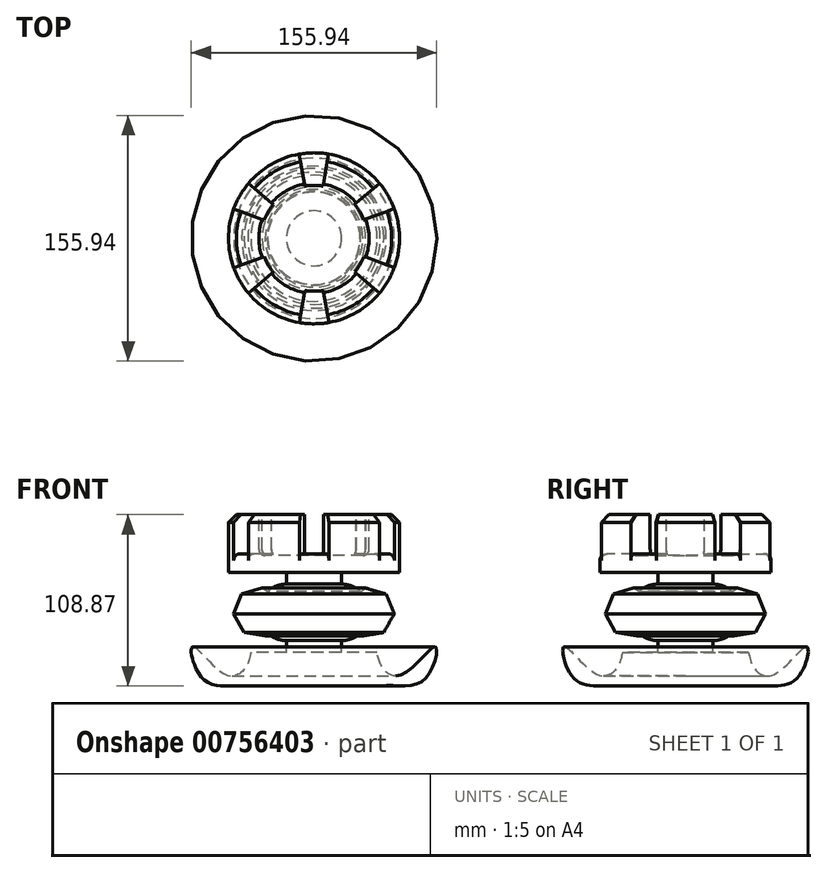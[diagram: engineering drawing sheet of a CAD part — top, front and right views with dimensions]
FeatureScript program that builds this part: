
annotation { "Feature Type Name" : "Feature", "Feature Type Description" : "" }
export const myFeature = defineFeature(function(context is Context, id is Id, definition is map)
    precondition{}
    {
        {
            var Q0;
            Q0=qCreatedBy(makeId("Front.planeOp"),FACE);
            var sketch = newSketch(context, id + "F0", { "sketchPlane" : qUnion([Q0])});
            skLineSegment(sketch, "E0", {"start": v(0, 0) * mm, "end": v(42.03, 0) * mm});
            skLineSegment(sketch, "E1", {"start": v(40.1, 21.45) * mm, "end": v(17.5, 21.45) * mm});
            skLineSegment(sketch, "E2", {"start": v(17.5, 21.45) * mm, "end": v(17.5, 28.86) * mm});
            skLineSegment(sketch, "E3", {"start": v(0, 108.87) * mm, "end": v(0, 0) * mm});
            skLineSegment(sketch, "E4", {"start": v(0, 108.87) * mm, "end": v(54.3, 108.87) * mm});
            skLineSegment(sketch, "E5", {"start": v(54.3, 108.87) * mm, "end": v(54.3, 72.1) * mm});
            skLineSegment(sketch, "E6", {"start": v(17.5, 72.1) * mm, "end": v(54.3, 72.1) * mm});
            skArc(sketch, "E7", {"start": v(17.5, 28.86) * mm, "mid": v(23.84, 30.02) * mm, "end": v(29.36, 33.35) * mm});
            skLineSegment(sketch, "E8.trimOffspring", {"start": v(17.5, 64.7) * mm, "end": v(17.5, 72.1) * mm});
            skLineSegment(sketch, "E9.0", {"start": v(50.96, 45.83) * mm, "end": v(44.36, 34.03) * mm});
            skLineSegment(sketch, "E9.1", {"start": v(44.36, 34.03) * mm, "end": v(31.03, 31.84) * mm});
            skLineSegment(sketch, "E9.2", {"start": v(31.03, 31.84) * mm, "end": v(29.36, 33.35) * mm});
            skLineSegment(sketch, "E9.4", {"start": v(29.7, 59.9) * mm, "end": v(32.89, 62.14) * mm});
            skLineSegment(sketch, "E9.5", {"start": v(32.89, 62.14) * mm, "end": v(45.85, 58.33) * mm});
            skLineSegment(sketch, "E9.6", {"start": v(45.85, 58.33) * mm, "end": v(50.96, 45.83) * mm});
            skPoint(sketch, "E9.0.midPoint", {"position": v(47.66, 39.93) * mm});
            skPoint(sketch, "E9.cCircle.center.orphan", {"position": v(35.42, 46.78) * mm});
            skArc(sketch, "E10.trimOffspring", {"start": v(29.7, 59.9) * mm, "mid": v(24.05, 63.45) * mm, "end": v(17.5, 64.7) * mm});
            skFitSpline(sketch, "E11", {"points": [v(42.03, 0) * mm, v(70.48, 4.44) * mm, v(77.04, 24.86) * mm, v(54.31, 6.63) * mm, v(40.1, 21.45) * mm], "startDerivative": vector(116, 13.94) * mm, "endDerivative": vector(-11.66, 114.4) * mm});
            skSolve(sketch);
        }
        {
            var Q0;
            Q0=makeQuery(id+"F0.imprint","IMPRINT",FACE,{"disambiguationData":[TD([[makeQuery(id+"F0.imprint","IMPRINT",EDGE,{"derivedFrom":sQuery(id+"F0.wireOp",EDGE,"E0")}),1.0]])]});
            var Q1;
            Q1=sQuery(id+"F0.wireOp",EDGE,"E3");
            revolve(context, id + "F1", {"surfaceOperationType" : NewSurfaceOperationType.NEW, "entities" : qUnion([Q0]), "axis" : qUnion([Q1]), "revolveType" : RevolveType.FULL});
        }
        {
            var Q0;
            Q0=makeQuery(id+"F1.opRevolve","SWEPT_FACE",FACE,{"disambiguationData":[OSD([sQuery(id+"F0.wireOp",EDGE,"E4")])]});
            var sketch = newSketch(context, id + "F2", { "sketchPlane" : qUnion([Q0])});
            skCircle(sketch, "E12", {"center": v(0, 0) * mm, "radius": 35 * mm});
            skSolve(sketch);
        }
        {
            var Q0;
            Q0=makeQuery(id+"F2.imprint","IMPRINT",FACE,{"disambiguationData":[TD([[makeQuery(id+"F2.imprint","IMPRINT",EDGE,{"derivedFrom":sQuery(id+"F2.wireOp",EDGE,"E12")}),1.0]])]});
            extrude(context, id + "F3", {"entities" : qUnion([Q0]), "operationType" : NewBodyOperationType.REMOVE, "oppositeDirection" : true, "depth" : 26 * mm, "offsetDistance" : 25 * mm});
        }
        {
            var Q0;
            Q0=makeQuery(id+"F1.opRevolve","SWEPT_FACE",FACE,{"disambiguationData":[OSD([sQuery(id+"F0.wireOp",EDGE,"E4")])]});
            var sketch = newSketch(context, id + "F4", { "sketchPlane" : qUnion([Q0])});
            skLineSegment(sketch, "E13", {"start": v(5.96, 34.49) * mm, "end": v(9.55, 55.3) * mm});
            skLineSegment(sketch, "E14", {"start": v(-6.08, 34.47) * mm, "end": v(-9.74, 55.26) * mm});
            skArc(sketch, "E15", {"start": v(5.96, 34.49) * mm, "mid": v(-0.06, 35) * mm, "end": v(-6.08, 34.47) * mm});
            skArc(sketch, "E16", {"start": v(9.55, 55.3) * mm, "mid": v(-0.1, 56.1) * mm, "end": v(-9.74, 55.26) * mm});
            skLineSegment(sketch, "E17.1.0", {"start": v(-26.9, 22.4) * mm, "end": v(-43.1, 35.91) * mm});
            skArc(sketch, "E17.1.1", {"start": v(-43.1, 35.91) * mm, "mid": v(-48.64, 27.97) * mm, "end": v(-52.72, 19.2) * mm});
            skLineSegment(sketch, "E17.1.2", {"start": v(-32.89, 11.97) * mm, "end": v(-52.72, 19.2) * mm});
            skArc(sketch, "E17.1.3", {"start": v(-26.9, 22.4) * mm, "mid": v(-30.34, 17.45) * mm, "end": v(-32.89, 11.97) * mm});
            skLineSegment(sketch, "E17.2.0", {"start": v(-32.85, -12.09) * mm, "end": v(-52.66, -19.38) * mm});
            skArc(sketch, "E17.2.1", {"start": v(-52.66, -19.38) * mm, "mid": v(-48.54, -28.14) * mm, "end": v(-42.98, -36.07) * mm});
            skLineSegment(sketch, "E17.2.2", {"start": v(-26.81, -22.5) * mm, "end": v(-42.98, -36.07) * mm});
            skArc(sketch, "E17.2.3", {"start": v(-32.85, -12.09) * mm, "mid": v(-30.28, -17.55) * mm, "end": v(-26.81, -22.5) * mm});
            skLineSegment(sketch, "E17.3.0", {"start": v(-5.96, -34.49) * mm, "end": v(-9.55, -55.3) * mm});
            skArc(sketch, "E17.3.1", {"start": v(-9.55, -55.3) * mm, "mid": v(0.1, -56.1) * mm, "end": v(9.74, -55.26) * mm});
            skLineSegment(sketch, "E17.3.2", {"start": v(6.08, -34.47) * mm, "end": v(9.74, -55.26) * mm});
            skArc(sketch, "E17.3.3", {"start": v(-5.96, -34.49) * mm, "mid": v(0.06, -35) * mm, "end": v(6.08, -34.47) * mm});
            skLineSegment(sketch, "E17.4.0", {"start": v(26.9, -22.4) * mm, "end": v(43.1, -35.91) * mm});
            skArc(sketch, "E17.4.1", {"start": v(43.1, -35.91) * mm, "mid": v(48.64, -27.97) * mm, "end": v(52.72, -19.2) * mm});
            skLineSegment(sketch, "E17.4.2", {"start": v(32.89, -11.97) * mm, "end": v(52.72, -19.2) * mm});
            skArc(sketch, "E17.4.3", {"start": v(26.9, -22.4) * mm, "mid": v(30.34, -17.45) * mm, "end": v(32.89, -11.97) * mm});
            skLineSegment(sketch, "E17.5.0", {"start": v(32.85, 12.09) * mm, "end": v(52.66, 19.38) * mm});
            skArc(sketch, "E17.5.1", {"start": v(52.66, 19.38) * mm, "mid": v(48.54, 28.14) * mm, "end": v(42.98, 36.07) * mm});
            skLineSegment(sketch, "E17.5.2", {"start": v(26.81, 22.5) * mm, "end": v(42.98, 36.07) * mm});
            skArc(sketch, "E17.5.3", {"start": v(32.85, 12.09) * mm, "mid": v(30.28, 17.55) * mm, "end": v(26.81, 22.5) * mm});
            skSolve(sketch);
        }
        {
            var Q0;
            Q0 = qSketchRegion(id + "F4", true);
            extrude(context, id + "F5", {"entities" : qUnion([Q0]), "operationType" : NewBodyOperationType.REMOVE, "oppositeDirection" : true, "depth" : 25 * mm, "offsetDistance" : 25 * mm});
        }
        {
            var Q0;
            {var subQ0=sQuery(id+"F0.wireOp",EDGE,"E4");var subQ1=sQuery(id+"F0.wireOp",EDGE,"E5");Q0=makeQuery(id+"F5.boolean.opBoolean","SPLIT",EDGE,{"disambiguationData":[TD([makeQuery(id+"F5.opExtrude","SWEPT_FACE",FACE,{"disambiguationData":[OSD([sQuery(id+"F4.wireOp",EDGE,"E17.3.2")])]})])],"derivedFrom":makeQuery(id+"F1.opRevolve","SWEPT_EDGE",EDGE,{"disambiguationData":[OSD([subQ0,subQ1])]})});}
            var Q1;
            {var subQ0=sQuery(id+"F0.wireOp",EDGE,"E4");var subQ1=sQuery(id+"F0.wireOp",EDGE,"E5");Q1=makeQuery(id+"F5.boolean.opBoolean","SPLIT",EDGE,{"disambiguationData":[TD([makeQuery(id+"F5.opExtrude","SWEPT_FACE",FACE,{"disambiguationData":[OSD([sQuery(id+"F4.wireOp",EDGE,"E17.4.2")])]})])],"derivedFrom":makeQuery(id+"F1.opRevolve","SWEPT_EDGE",EDGE,{"disambiguationData":[OSD([subQ0,subQ1])]})});}
            var Q2;
            {var subQ0=sQuery(id+"F0.wireOp",EDGE,"E4");var subQ1=sQuery(id+"F0.wireOp",EDGE,"E5");Q2=makeQuery(id+"F5.boolean.opBoolean","SPLIT",EDGE,{"disambiguationData":[TD([makeQuery(id+"F5.opExtrude","SWEPT_FACE",FACE,{"disambiguationData":[OSD([sQuery(id+"F4.wireOp",EDGE,"E13")])]})])],"derivedFrom":makeQuery(id+"F1.opRevolve","SWEPT_EDGE",EDGE,{"disambiguationData":[OSD([subQ0,subQ1])]})});}
            var Q3;
            {var subQ0=sQuery(id+"F0.wireOp",EDGE,"E4");var subQ1=sQuery(id+"F0.wireOp",EDGE,"E5");Q3=makeQuery(id+"F5.boolean.opBoolean","SPLIT",EDGE,{"disambiguationData":[TD([makeQuery(id+"F5.opExtrude","SWEPT_FACE",FACE,{"disambiguationData":[OSD([sQuery(id+"F4.wireOp",EDGE,"E14")])]})])],"derivedFrom":makeQuery(id+"F1.opRevolve","SWEPT_EDGE",EDGE,{"disambiguationData":[OSD([subQ0,subQ1])]})});}
            var Q4;
            {var subQ0=sQuery(id+"F0.wireOp",EDGE,"E4");var subQ1=sQuery(id+"F0.wireOp",EDGE,"E5");Q4=makeQuery(id+"F5.boolean.opBoolean","SPLIT",EDGE,{"disambiguationData":[TD([makeQuery(id+"F5.opExtrude","SWEPT_FACE",FACE,{"disambiguationData":[OSD([sQuery(id+"F4.wireOp",EDGE,"E17.1.2")])]})])],"derivedFrom":makeQuery(id+"F1.opRevolve","SWEPT_EDGE",EDGE,{"disambiguationData":[OSD([subQ0,subQ1])]})});}
            var Q5;
            {var subQ0=sQuery(id+"F0.wireOp",EDGE,"E4");var subQ1=sQuery(id+"F0.wireOp",EDGE,"E5");Q5=makeQuery(id+"F5.boolean.opBoolean","SPLIT",EDGE,{"disambiguationData":[TD([makeQuery(id+"F5.opExtrude","SWEPT_FACE",FACE,{"disambiguationData":[OSD([sQuery(id+"F4.wireOp",EDGE,"E17.2.2")])]})])],"derivedFrom":makeQuery(id+"F1.opRevolve","SWEPT_EDGE",EDGE,{"disambiguationData":[OSD([subQ0,subQ1])]})});}
            chamfer(context, id + "F6", {"entities" : qUnion([Q0, Q1, Q2, Q3, Q4, Q5]), "width" : 5 * mm, "tangentPropagation" : true});
        }
        {
            var Q0;
            Q0=makeQuery(id+"F5.boolean.opBoolean","INTERSECT",EDGE,{"derivedFrom":[makeQuery(id+"F1.opRevolve","SWEPT_FACE",FACE,{"disambiguationData":[OSD([sQuery(id+"F0.wireOp",EDGE,"E5")])]}),makeQuery(id+"F5.opExtrude","CAP_FACE",FACE,{"disambiguationData":[OSD([sQuery(id+"F4.wireOp",EDGE,"E17.3.0"),sQuery(id+"F4.wireOp",EDGE,"E17.3.1"),sQuery(id+"F4.wireOp",EDGE,"E17.3.2"),sQuery(id+"F4.wireOp",EDGE,"E17.3.3")])],"isStart":false})]});
            var Q1;
            Q1=makeQuery(id+"F5.boolean.opBoolean","INTERSECT",EDGE,{"derivedFrom":[makeQuery(id+"F1.opRevolve","SWEPT_FACE",FACE,{"disambiguationData":[OSD([sQuery(id+"F0.wireOp",EDGE,"E5")])]}),makeQuery(id+"F5.opExtrude","CAP_FACE",FACE,{"disambiguationData":[OSD([sQuery(id+"F4.wireOp",EDGE,"E17.4.0"),sQuery(id+"F4.wireOp",EDGE,"E17.4.1"),sQuery(id+"F4.wireOp",EDGE,"E17.4.2"),sQuery(id+"F4.wireOp",EDGE,"E17.4.3")])],"isStart":false})]});
            var Q2;
            Q2=makeQuery(id+"F5.boolean.opBoolean","INTERSECT",EDGE,{"derivedFrom":[makeQuery(id+"F1.opRevolve","SWEPT_FACE",FACE,{"disambiguationData":[OSD([sQuery(id+"F0.wireOp",EDGE,"E5")])]}),makeQuery(id+"F5.opExtrude","CAP_FACE",FACE,{"disambiguationData":[OSD([sQuery(id+"F4.wireOp",EDGE,"E17.5.0"),sQuery(id+"F4.wireOp",EDGE,"E17.5.1"),sQuery(id+"F4.wireOp",EDGE,"E17.5.2"),sQuery(id+"F4.wireOp",EDGE,"E17.5.3")])],"isStart":false})]});
            var Q3;
            Q3=makeQuery(id+"F5.boolean.opBoolean","INTERSECT",EDGE,{"derivedFrom":[makeQuery(id+"F1.opRevolve","SWEPT_FACE",FACE,{"disambiguationData":[OSD([sQuery(id+"F0.wireOp",EDGE,"E5")])]}),makeQuery(id+"F5.opExtrude","CAP_FACE",FACE,{"disambiguationData":[OSD([sQuery(id+"F4.wireOp",EDGE,"E13"),sQuery(id+"F4.wireOp",EDGE,"E14"),sQuery(id+"F4.wireOp",EDGE,"E15"),sQuery(id+"F4.wireOp",EDGE,"E16")])],"isStart":false})]});
            var Q4;
            Q4=makeQuery(id+"F5.boolean.opBoolean","INTERSECT",EDGE,{"derivedFrom":[makeQuery(id+"F1.opRevolve","SWEPT_FACE",FACE,{"disambiguationData":[OSD([sQuery(id+"F0.wireOp",EDGE,"E5")])]}),makeQuery(id+"F5.opExtrude","CAP_FACE",FACE,{"disambiguationData":[OSD([sQuery(id+"F4.wireOp",EDGE,"E17.1.0"),sQuery(id+"F4.wireOp",EDGE,"E17.1.1"),sQuery(id+"F4.wireOp",EDGE,"E17.1.2"),sQuery(id+"F4.wireOp",EDGE,"E17.1.3")])],"isStart":false})]});
            var Q5;
            Q5=makeQuery(id+"F5.boolean.opBoolean","INTERSECT",EDGE,{"derivedFrom":[makeQuery(id+"F1.opRevolve","SWEPT_FACE",FACE,{"disambiguationData":[OSD([sQuery(id+"F0.wireOp",EDGE,"E5")])]}),makeQuery(id+"F5.opExtrude","CAP_FACE",FACE,{"disambiguationData":[OSD([sQuery(id+"F4.wireOp",EDGE,"E17.2.0"),sQuery(id+"F4.wireOp",EDGE,"E17.2.1"),sQuery(id+"F4.wireOp",EDGE,"E17.2.2"),sQuery(id+"F4.wireOp",EDGE,"E17.2.3")])],"isStart":false})]});
            var Q6;
            Q6=makeQuery(id+"F3.boolean.opBoolean","COPY",EDGE,{"derivedFrom":makeQuery(id+"F3.opExtrude","CAP_EDGE",EDGE,{"disambiguationData":[OSD([sQuery(id+"F2.wireOp",EDGE,"E12")])],"isStart":false})});
            fillet(context, id + "F7", {"entities" : qUnion([Q0, Q1, Q2, Q3, Q4, Q5, Q6]), "radius" : 4 * mm, "tangentPropagation" : true, "allowEdgeOverflow" : false});
        }
    });
